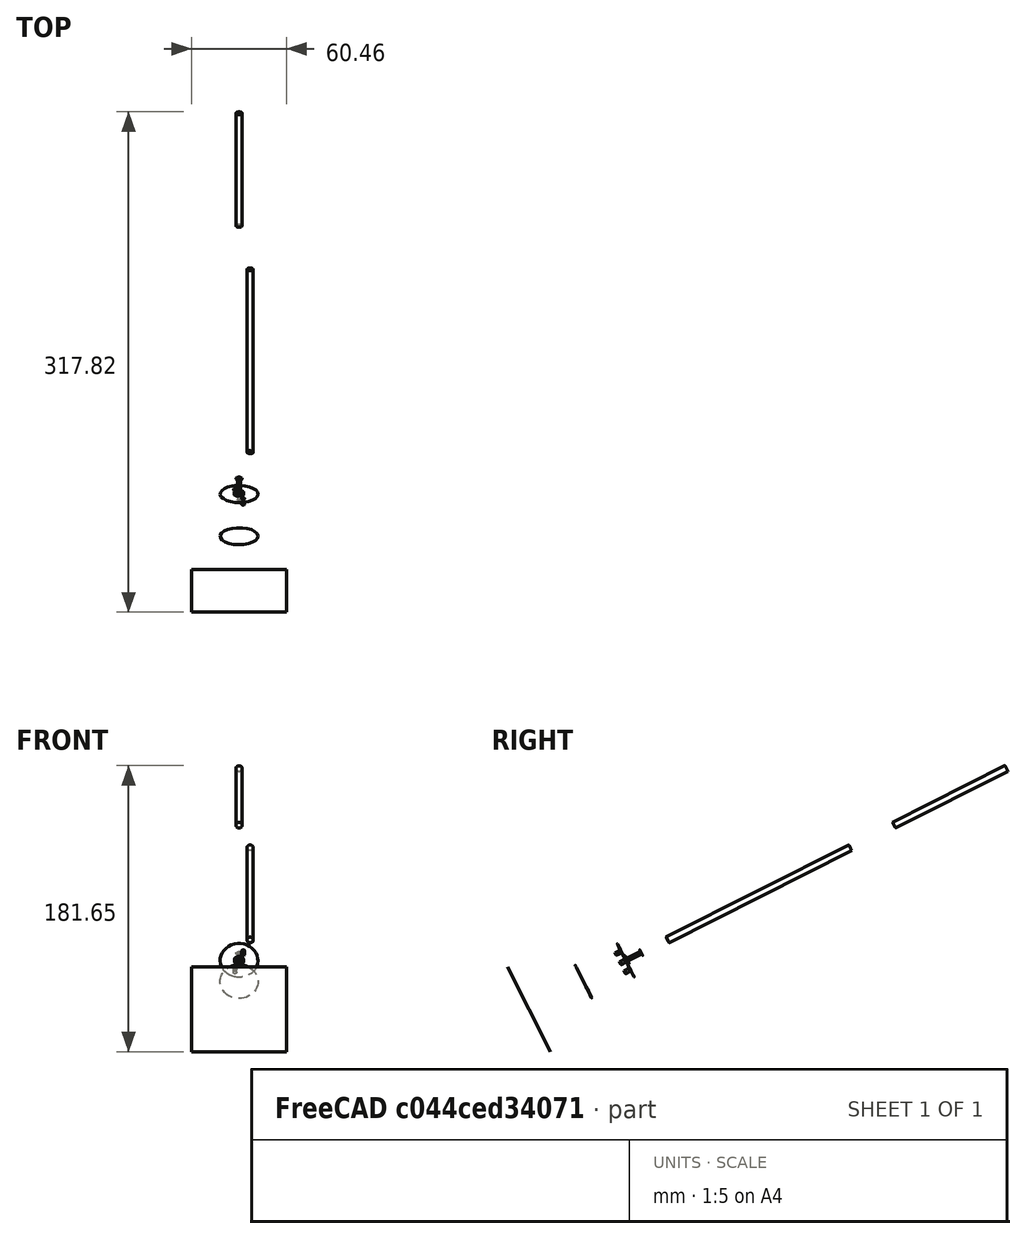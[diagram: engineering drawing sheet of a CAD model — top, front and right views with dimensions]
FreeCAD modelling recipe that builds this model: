
FCSTD DOCUMENT  (FreeCAD 0.19R24366 (Git))
Label: sailface_prop_motor_assembly
License: All rights reserved
LicenseURL: http://en.wikipedia.org/wiki/All_rights_reserved
objects: App::FeaturePython×23, Part::FeaturePython×17, App::Link×4
note: 16 computed .brp shape members not serialized (recipe doc carries the construction recipe); baked Part::Feature solids carry a one-line shape summary decoded from their .brp
EXTERNAL_REF file=Prop_uxcell_prop_shaft.FCStd obj=Part
EXTERNAL_REF file=Prop_uxcell_prop_shaft.FCStd obj=Part001
EXTERNAL_REF file=Prop_uxcell_prop_shaft.FCStd obj=Part002
EXTERNAL_REF file=MotorAndHolder_v1.FCStd obj=Part

FEATURE [App::Link] Link004  label="PropShaftSleeve"
  LinkPlacement = pos=(-1.04194e-10,303.325,152.862) rot=(0.782097,-0.530606,0.326776;2.24386rad)
  LinkedObject = -> <external Prop_uxcell_prop_shaft.FCStd>#Part
  Placement = pos=(-1.04194e-10,303.325,152.862) rot=(0.782097,-0.530606,0.326776;2.24386rad)
FEATURE [App::Link] Link005  label="PropAndShaft"
  LinkPlacement = pos=(1.45925,156.515,79.2819) rot=(0.211549,0.512519,0.832209;3.80335rad)
  LinkedObject = -> <external Prop_uxcell_prop_shaft.FCStd>#Part001
  Placement = pos=(1.45925,156.515,79.2819) rot=(0.211549,0.512519,0.832209;3.80335rad)
FEATURE [App::Link] Link015  label="ShaftConnectorTemp"
  LinkPlacement = pos=(1.74213e-10,0,0) rot=(-0.752268,-0.345496,-0.561003;1.37203rad)
  LinkedObject = -> <external Prop_uxcell_prop_shaft.FCStd>#Part002
  Placement = pos=(1.74213e-10,0,0) rot=(-0.752268,-0.345496,-0.561003;1.37203rad)
FEATURE [App::Link] Link014  label="MotorPart"
  LinkPlacement = pos=(9.7944e-11,0,0) rot=(-0.332635,0.494526,0.802993;2.15114rad)
  LinkedObject = -> <external MotorAndHolder_v1.FCStd>#Part
  Placement = pos=(9.7944e-11,0,0) rot=(-0.332635,0.494526,0.802993;2.15114rad)
FEATURE [Part::FeaturePython] Workplane  # WARN: FeaturePython — macro-defined, semantics opaque (R4)
  Fixed = true
  Length = 60.4603
  Placement = pos=(0,0,0) rot=(1,0,0;2.0376rad)
  Width = 60.4603
FEATURE [Part::FeaturePython] Parts001  # WARN: FeaturePython — macro-defined, semantics opaque (R4)
  Group = -> [Link014,Link015,Link005,Link004,Workplane]
  GroupMode = 0
FEATURE [Part::FeaturePython] _Element043  # link proxy (typed FeaturePython)
  Detach = false
  LinkTransform = true
  LinkedObject = -> Link004 [Extrude.Face2]
  _Parent = -> Elements001
FEATURE [App::FeaturePython] ElementLink018  label="_Element043"  # link proxy (typed FeaturePython)
  LinkTransform = true
  LinkedObject = -> _Element043
  _Parent = -> Constraint008
FEATURE [Part::FeaturePython] _Element044  # link proxy (typed FeaturePython)
  Detach = false
  LinkTransform = true
  LinkedObject = -> Link005 [Extrude002.Face1]
  _Parent = -> Elements001
FEATURE [App::FeaturePython] ElementLink019  label="_Element044"  # link proxy (typed FeaturePython)
  LinkTransform = true
  LinkedObject = -> _Element044
  _Parent = -> Constraint008
FEATURE [App::FeaturePython] Constraint008  label="AxialAlignment002"  # WARN: FeaturePython — macro-defined, semantics opaque (R4)
  Angle = 0
  AnglePitch = 0
  AngleRoll = 0
  Disabled = false
  Group = -> [ElementLink018,ElementLink019]
  LockAngle = false
  Multiply = false
  _ConstraintType = 36
  _Parent = -> Constraints001
FEATURE [App::FeaturePython] ElementLink020  label="_Element044"  # link proxy (typed FeaturePython)
  LinkTransform = true
  LinkedObject = -> _Element044
  _Parent = -> Constraint009
FEATURE [App::FeaturePython] ElementLink021  label="_Element043"  # link proxy (typed FeaturePython)
  LinkTransform = true
  LinkedObject = -> _Element043
  _Parent = -> Constraint009
FEATURE [App::FeaturePython] Constraint009  label="AxialAlignment"  # WARN: FeaturePython — macro-defined, semantics opaque (R4)
  Angle = 0
  AnglePitch = 0
  AngleRoll = 0
  Disabled = false
  Group = -> [ElementLink020,ElementLink021]
  LockAngle = false
  Multiply = false
  _ConstraintType = 36
  _Parent = -> Constraints001
FEATURE [Part::FeaturePython] _Element046  # link proxy (typed FeaturePython)
  Detach = false
  LinkTransform = true
  LinkedObject = -> Link005 [Extrude002.Face3]
  _Parent = -> Elements001
FEATURE [Part::FeaturePython] _Element045  # link proxy (typed FeaturePython)
  Detach = false
  LinkTransform = true
  LinkedObject = -> Link015 [Body.Pocket001.Face7]
  _Parent = -> Elements001
FEATURE [Part::FeaturePython] _Element047  # link proxy (typed FeaturePython)
  Detach = false
  LinkTransform = true
  LinkedObject = -> Link014 [Body.Pocket.Face11]
  _Parent = -> Elements001
FEATURE [Part::FeaturePython] _Element048  # link proxy (typed FeaturePython)
  Detach = false
  LinkTransform = true
  LinkedObject = -> Link015 [Body.Pocket001.Face6]
  _Parent = -> Elements001
FEATURE [App::FeaturePython] Constraints001  # WARN: FeaturePython — macro-defined, semantics opaque (R4)
  Group = -> [Constraint008,Constraint009,Constraint,Constraint010,Constraint011,Constraint012,Constraint013]
  _Version = 1
FEATURE [App::FeaturePython] Elements001  # WARN: FeaturePython — macro-defined, semantics opaque (R4)
  Group = -> [_Element043,_Element044,_Element045,_Element046,_Element047,_Element048,Element,Element001,Element002,Element003,Element004,_Element,_Element049,_Element050]
FEATURE [Part::FeaturePython] Assembly001  label="PropMotorAssembly"  # WARN: FeaturePython — macro-defined, semantics opaque (R4)
  AutoRelax = true
  BuildShape = 0
  Freeze = false
  Group = -> [Constraints001,Parts001,Elements001]
  Verbose = false
  _SolverType = 1
  _Version = 1
FEATURE [Part::FeaturePython] Element  # link proxy (typed FeaturePython)
  Detach = false
  LinkTransform = true
  LinkedObject = -> Link014 [Body.Pocket.Face5]
  _Parent = -> Elements001
FEATURE [Part::FeaturePython] Element001  # link proxy (typed FeaturePython)
  Detach = false
  LinkTransform = true
  LinkedObject = -> Link014 [Body.Pocket.Face3]
  _Parent = -> Elements001
FEATURE [Part::FeaturePython] Element002  # link proxy (typed FeaturePython)
  Detach = false
  LinkTransform = true
  LinkedObject = -> Link014 [Body.Pocket.Face10]
  _Parent = -> Elements001
FEATURE [Part::FeaturePython] Element003  # link proxy (typed FeaturePython)
  Detach = false
  LinkTransform = true
  LinkedObject = -> Link014 [Body.Pocket.Face6]
  _Parent = -> Elements001
FEATURE [Part::FeaturePython] Element004  # link proxy (typed FeaturePython)
  Detach = false
  LinkTransform = true
  LinkedObject = -> Link014 [Body.Pocket.Face4]
  _Parent = -> Elements001
FEATURE [App::FeaturePython] Constraint  label="AxialAlignment003"  # WARN: FeaturePython — macro-defined, semantics opaque (R4)
  Angle = 0
  AnglePitch = 0
  AngleRoll = 0
  Disabled = false
  Group = -> [ElementLink,ElementLink022]
  LockAngle = false
  Multiply = false
  _ConstraintType = 36
  _Parent = -> Constraints001
FEATURE [App::FeaturePython] ElementLink  label="_Element"  # link proxy (typed FeaturePython)
  LinkTransform = true
  LinkedObject = -> _Element
  _Parent = -> Constraint
FEATURE [Part::FeaturePython] _Element  # link proxy (typed FeaturePython)
  Detach = false
  LinkTransform = true
  LinkedObject = -> Link015 [Body.Pocket001.Face4]
  _Parent = -> Elements001
FEATURE [App::FeaturePython] ElementLink022  label="Element002"  # link proxy (typed FeaturePython)
  LinkTransform = true
  LinkedObject = -> Element002
  _Parent = -> Constraint
FEATURE [App::FeaturePython] Constraint010  label="AxialAlignment004"  # WARN: FeaturePython — macro-defined, semantics opaque (R4)
  Angle = 0
  AnglePitch = 0
  AngleRoll = 0
  Disabled = false
  Group = -> [ElementLink023,ElementLink024]
  LockAngle = false
  Multiply = false
  _ConstraintType = 36
  _Parent = -> Constraints001
FEATURE [App::FeaturePython] ElementLink023  label="_Element044"  # link proxy (typed FeaturePython)
  LinkTransform = true
  LinkedObject = -> _Element044
  _Parent = -> Constraint010
FEATURE [App::FeaturePython] ElementLink024  label="_Element"  # link proxy (typed FeaturePython)
  LinkTransform = true
  LinkedObject = -> _Element
  _Parent = -> Constraint010
FEATURE [App::FeaturePython] Constraint011  label="AxialAlignment005"  # WARN: FeaturePython — macro-defined, semantics opaque (R4)
  Angle = 0
  AnglePitch = 0
  AngleRoll = 0
  Disabled = false
  Group = -> [ElementLink025,ElementLink026]
  LockAngle = false
  Multiply = false
  _ConstraintType = 36
  _Parent = -> Constraints001
FEATURE [App::FeaturePython] ElementLink025  label="_Element049"  # link proxy (typed FeaturePython)
  LinkTransform = true
  LinkedObject = -> _Element049
  _Parent = -> Constraint011
FEATURE [Part::FeaturePython] _Element049  # link proxy (typed FeaturePython)
  Detach = false
  LinkTransform = true
  LinkedObject = -> Workplane [Face1]
  _Parent = -> Elements001
FEATURE [App::FeaturePython] ElementLink026  label="_Element050"  # link proxy (typed FeaturePython)
  LinkTransform = true
  LinkedObject = -> _Element050
  _Parent = -> Constraint011
FEATURE [Part::FeaturePython] _Element050  # link proxy (typed FeaturePython)
  Detach = false
  LinkTransform = true
  LinkedObject = -> Link014 [Body.Pocket.Face2]
  _Parent = -> Elements001
FEATURE [App::FeaturePython] Constraint012  label="PlaneCoincident"  # WARN: FeaturePython — macro-defined, semantics opaque (R4)
  Angle = 0
  AnglePitch = 0
  AngleRoll = 0
  Cascade = false
  Disabled = false
  Group = -> [ElementLink027,ElementLink028]
  LockAngle = false
  Multiply = false
  OffsetX = 0
  OffsetY = 0
  _ConstraintType = 35
  _Parent = -> Constraints001
FEATURE [App::FeaturePython] ElementLink027  label="_Element047"  # link proxy (typed FeaturePython)
  LinkTransform = true
  LinkedObject = -> _Element047
  _Parent = -> Constraint012
FEATURE [App::FeaturePython] ElementLink028  label="_Element045"  # link proxy (typed FeaturePython)
  LinkTransform = true
  LinkedObject = -> _Element045
  _Parent = -> Constraint012
FEATURE [App::FeaturePython] Constraint013  label="PlaneCoincident001"  # WARN: FeaturePython — macro-defined, semantics opaque (R4)
  Angle = 0
  AnglePitch = 0
  AngleRoll = 0
  Cascade = false
  Disabled = true
  Group = -> [ElementLink029,ElementLink030]
  LockAngle = false
  Multiply = false
  OffsetX = 0
  OffsetY = 0
  _ConstraintType = 35
  _Parent = -> Constraints001
FEATURE [App::FeaturePython] ElementLink029  label="_Element046"  # link proxy (typed FeaturePython)
  LinkTransform = true
  LinkedObject = -> _Element046
  _Parent = -> Constraint013
FEATURE [App::FeaturePython] ElementLink030  label="_Element045"  # link proxy (typed FeaturePython)
  LinkTransform = true
  LinkedObject = -> _Element045
  _Parent = -> Constraint013

RESOLVED EXTERNAL PARTS (link-assembly join: the EXTERNAL_REF files above that resolve inside this repo's crawl, each included once):
---- part MotorAndHolder_v1.FCStd = doc fcstd_ec45f42837d4 ----
FCSTD DOCUMENT  (FreeCAD 0.19R24366 (Git))
Label: MotorAndHolder_v1
License: All rights reserved
LicenseURL: http://en.wikipedia.org/wiki/All_rights_reserved
objects: Sketcher::SketchObject×16, PartDesign::Pad×9, PartDesign::Pocket×9, PartDesign::Body×4, App::Part×4, Mesh::Feature×1
note: 56 computed .brp shape members not serialized (recipe doc carries the construction recipe); baked Part::Feature solids carry a one-line shape summary decoded from their .brp

FEATURE [Sketcher::SketchObject] Sketch
  FullyConstrained = false
  MapMode = 5
  Support = -> [XY_Plane001]
  sketch-geometry (1):
    g0: Circle CenterX=0 CenterY=0 CenterZ=0 NormalX=0 NormalY=0 NormalZ=1 AngleXU=0 Radius=12
  constraints (1):
    c: Radius(g0) = 12
FEATURE [PartDesign::Pad] Pad  label="MotorMain"
  Direction = (1,1,1)
  Length = 30
  Length2 = 100
  Profile = -> Sketch
  Type = 0
FEATURE [Sketcher::SketchObject] Sketch001
  FullyConstrained = true
  MapMode = 5
  Placement = pos=(0,0,30) rot=(0,0,1;0rad)
  Support = -> [Pad]
  sketch-geometry (1):
    g0: Circle CenterX=0 CenterY=0 CenterZ=0 NormalX=0 NormalY=0 NormalZ=1 AngleXU=0 Radius=3
  constraints (2):
    c: Coincident(g0,g-1)
    c: Radius(g0) = 3
FEATURE [PartDesign::Pad] Pad001  label="MotorHeader"
  BaseFeature = -> Pad
  Direction = (1,1,1)
  Length = 1
  Length2 = 100
  Profile = -> Sketch001
  Type = 0
FEATURE [Sketcher::SketchObject] Sketch002
  FullyConstrained = true
  MapMode = 5
  Placement = pos=(0,0,31) rot=(0,0,1;0rad)
  Support = -> [Pad001]
  sketch-geometry (1):
    g0: Circle CenterX=0 CenterY=0 CenterZ=0 NormalX=0 NormalY=0 NormalZ=1 AngleXU=0 Radius=1
  constraints (2):
    c: Coincident(g0,g-1)
    c: Radius(g0) = 1
FEATURE [PartDesign::Pad] Pad002  label="Shaft"
  BaseFeature = -> Pad001
  Direction = (1,1,1)
  Length = 10
  Length2 = 100
  Profile = -> Sketch002
  Type = 0
FEATURE [Sketcher::SketchObject] Sketch003
  FullyConstrained = true
  MapMode = 5
  Placement = pos=(0,0,30) rot=(0,0,1;0rad)
  Support = -> [Pad002]
  sketch-geometry (4):
    g0: Circle CenterX=-7 CenterY=0 CenterZ=0 NormalX=0 NormalY=0 NormalZ=1 AngleXU=0 Radius=1
    g1: Circle CenterX=7 CenterY=0 CenterZ=0 NormalX=0 NormalY=0 NormalZ=1 AngleXU=0 Radius=1
    g2: LineSegment StartX=-7 StartY=0 StartZ=0 EndX=0 EndY=0 EndZ=0
    g3: LineSegment StartX=0 StartY=0 StartZ=0 EndX=7 EndY=0 EndZ=0
  constraints (10):
    c: PointOnObject(g0,g-1)
    c: PointOnObject(g1,g-1)
    c: Diameter(g1) = 2
    c: Diameter(g0) = 2
    c: Coincident(g2,g0)
    c: Coincident(g2,g-1)
    c: Coincident(g3,g2)
    c: Coincident(g3,g1)
    c: Equal(g3,g2)
    c: DistanceX(g2,g2) = 7
FEATURE [PartDesign::Pocket] Pocket
  BaseFeature = -> Pad002
  Length = 4
  Length2 = 100
  Profile = -> Sketch003
  Type = 0
FEATURE [PartDesign::Body] Body  label="MotorBody"
  Group = -> [Sketch,Pad,Sketch001,Pad001,Sketch002,Pad002,Sketch003,Pocket]
  Origin = -> Origin001
  Tip = -> Pocket
FEATURE [App::Part] Part  label="MotorPart"
  Group = -> [Body]
  Origin = -> Origin
FEATURE [Sketcher::SketchObject] Sketch004
  FullyConstrained = false
  Placement = pos=(0,0,30) rot=(0,0,1;0rad)
  sketch-geometry (6):
    g0: LineSegment StartX=-15 StartY=2.95461 StartZ=0 EndX=15 EndY=2.95461 EndZ=0
    g1: LineSegment StartX=15 StartY=2.95461 StartZ=0 EndX=15 EndY=-13.0454 EndZ=0
    g2: LineSegment StartX=15 StartY=-13.0454 StartZ=0 EndX=-15 EndY=-13.0454 EndZ=0
    g3: LineSegment StartX=-15 StartY=-13.0454 StartZ=0 EndX=-15 EndY=2.95461 EndZ=0
    g4: LineSegment StartX=-15 StartY=0 StartZ=0 EndX=0 EndY=0 EndZ=0
    g5: LineSegment StartX=0 StartY=0 StartZ=0 EndX=15 EndY=0 EndZ=0
  constraints (17):
    c: Coincident(g0,g1)
    c: Coincident(g1,g2)
    c: Coincident(g2,g3)
    c: Coincident(g3,g0)
    c: Horizontal(g0)
    c: Horizontal(g2)
    c: Vertical(g1)
    c: Vertical(g3)
    c: DistanceY(g1,g1) = 16
    c: DistanceX(g0,g0) = 30
    c: PointOnObject(g4,g3)
    c: Coincident(g4,g-1)
    c: Horizontal(g4)
    c: PointOnObject(g5,g1)
    c: Horizontal(g5)
    c: Equal(g4,g5)
    c: Coincident(g5,g-1)
FEATURE [PartDesign::Pad] Pad003
  Direction = (1,1,1)
  Length = 2
  Length2 = 100
  Placement = pos=(0,0,30) rot=(0,0,1;0rad)
  Profile = -> Sketch004
  Type = 0
FEATURE [Sketcher::SketchObject] Sketch005
  FullyConstrained = true
  MapMode = 5
  Placement = pos=(0,0,30) rot=(0,0,1;0rad)
  Support = -> [Pad]
  sketch-geometry (1):
    g0: Circle CenterX=0 CenterY=0 CenterZ=0 NormalX=0 NormalY=0 NormalZ=1 AngleXU=0 Radius=3.4
  constraints (2):
    c: Coincident(g0,g-1)
    c: Radius(g0) = 3.4
FEATURE [PartDesign::Pocket] Pocket001
  BaseFeature = -> Pad003
  Length = 20
  Length2 = 100
  Placement = pos=(0,0,30) rot=(0,0,1;0rad)
  Profile = -> Sketch005
  Reversed = true
  Type = 0
FEATURE [PartDesign::Pad] Pad004
  BaseFeature = -> Pocket001
  Direction = (1,1,1)
  Length = 25
  Length2 = 100
  Placement = pos=(0,0,30) rot=(0,0,1;0rad)
  Profile = -> Sketch004
  Reversed = true
  Type = 0
FEATURE [Sketcher::SketchObject] Sketch006
  FullyConstrained = false
  MapMode = 5
  Support = -> [XY_Plane003]
  sketch-geometry (1):
    g0: Circle CenterX=0 CenterY=0 CenterZ=0 NormalX=0 NormalY=0 NormalZ=1 AngleXU=0 Radius=12.2
  constraints (1):
    c: Radius(g0) = 12.2
FEATURE [PartDesign::Pocket] Pocket002
  BaseFeature = -> Pad004
  Length = 30
  Length2 = 100
  Placement = pos=(0,0,30) rot=(0,0,1;0rad)
  Profile = -> Sketch006
  Reversed = true
  Type = 0
FEATURE [Sketcher::SketchObject] Sketch007
  FullyConstrained = false
  MapMode = 5
  Placement = pos=(0,0,32) rot=(0,0,1;0rad)
  Support = -> [Pocket002]
  sketch-geometry (4):
    g0: Circle CenterX=-7.01627 CenterY=0 CenterZ=0 NormalX=0 NormalY=0 NormalZ=1 AngleXU=0 Radius=1.2
    g1: Circle CenterX=7.01627 CenterY=0 CenterZ=0 NormalX=0 NormalY=0 NormalZ=1 AngleXU=0 Radius=1.1
    g2: LineSegment StartX=-7.01627 StartY=0 StartZ=0 EndX=0 EndY=0 EndZ=0
    g3: LineSegment StartX=0 StartY=0 StartZ=0 EndX=7.01627 EndY=0 EndZ=0
  constraints (9):
    c: PointOnObject(g0,g-1)
    c: PointOnObject(g1,g-1)
    c: Diameter(g1) = 2.2
    c: Diameter(g0) = 2.4
    c: Coincident(g2,g0)
    c: Coincident(g2,g-1)
    c: Coincident(g3,g2)
    c: Coincident(g3,g1)
    c: Equal(g3,g2)
FEATURE [PartDesign::Pocket] Pocket003
  BaseFeature = -> Pocket002
  Length = 5
  Length2 = 100
  Placement = pos=(0,0,30) rot=(0,0,1;0rad)
  Profile = -> Sketch007
  Type = 0
FEATURE [Sketcher::SketchObject] Sketch008
  FullyConstrained = false
  MapMode = 5
  Placement = pos=(0,0,32) rot=(0,0,1;0rad)
  Support = -> [Pocket003]
  sketch-geometry (4):
    g0: Circle CenterX=-10 CenterY=-10.9518 CenterZ=0 NormalX=0 NormalY=0 NormalZ=1 AngleXU=0 Radius=1.4
    g1: Circle CenterX=10 CenterY=-10.9518 CenterZ=0 NormalX=0 NormalY=0 NormalZ=1 AngleXU=0 Radius=1.4
    g2: LineSegment StartX=10 StartY=-10.9518 StartZ=0 EndX=0 EndY=-10.9518 EndZ=0
    g3: LineSegment StartX=-10 StartY=-10.9518 StartZ=0 EndX=0 EndY=-10.9518 EndZ=0
  constraints (10):
    c: Horizontal(g1,g0)
    c: Coincident(g2,g1)
    c: PointOnObject(g2,g-2)
    c: Horizontal(g2)
    c: Coincident(g3,g0)
    c: Coincident(g3,g2)
    c: Equal(g2,g3)
    c: DistanceX(g0,g1) = 20
    c: Equal(g0,g1)
    c: Diameter(g0) = 2.8
FEATURE [PartDesign::Pocket] Pocket004
  BaseFeature = -> Pocket003
  Length = 50
  Length2 = 100
  Placement = pos=(0,0,30) rot=(0,0,1;0rad)
  Profile = -> Sketch008
  Type = 0
FEATURE [PartDesign::Body] Body001  label="MotorHolderBody"
  Group = -> [Sketch004,Pad003,Sketch005,Pocket001,Pad004,Sketch006,Pocket002,Sketch007,Pocket003,Sketch008,Pocket004]
  Origin = -> Origin003
  Tip = -> Pocket004
FEATURE [App::Part] Part001  label="MotorHolder"
  Group = -> [Body001]
  Origin = -> Origin002
FEATURE [Mesh::Feature] Mesh  label="MotorHolder (Meshed)"
FEATURE [Sketcher::SketchObject] Sketch013
  FullyConstrained = true
  MapMode = 5
  Support = -> [XY_Plane012]
  sketch-geometry (1):
    g0: Circle CenterX=0 CenterY=0 CenterZ=0 NormalX=0 NormalY=0 NormalZ=1 AngleXU=0 Radius=1.25
  constraints (2):
    c: Coincident(g0,g-1)
    c: Diameter(g0) = 2.5
FEATURE [PartDesign::Pad] Pad006
  Direction = (1,1,1)
  Length = 200
  Length2 = 100
  Profile = -> Sketch013
  Type = 0
FEATURE [PartDesign::Body] Body006
  Group = -> [Sketch013,Pad006]
  Origin = -> Origin012
  Tip = -> Pad006
FEATURE [App::Part] Part006  label="ConnectorRod2.5x200mm001"
  Group = -> [Body006]
  Origin = -> Origin013
FEATURE [Sketcher::SketchObject] Sketch014
  FullyConstrained = false
  MapMode = 5
  Support = -> [XY_Plane015]
  sketch-geometry (1):
    g0: Circle CenterX=0 CenterY=0 CenterZ=0 NormalX=0 NormalY=0 NormalZ=1 AngleXU=0 Radius=12
  constraints (1):
    c: Radius(g0) = 12
FEATURE [PartDesign::Pad] Pad007  label="MotorMain001"
  Direction = (1,1,1)
  Length = 30
  Length2 = 100
  Profile = -> Sketch014
  Type = 0
FEATURE [Sketcher::SketchObject] Sketch017
  FullyConstrained = false
  Placement = pos=(0,0,30) rot=(0,0,1;0rad)
  sketch-geometry (6):
    g0: LineSegment StartX=-15 StartY=2.95461 StartZ=0 EndX=15 EndY=2.95461 EndZ=0
    g1: LineSegment StartX=15 StartY=2.95461 StartZ=0 EndX=15 EndY=-13.0454 EndZ=0
    g2: LineSegment StartX=15 StartY=-13.0454 StartZ=0 EndX=-15 EndY=-13.0454 EndZ=0
    g3: LineSegment StartX=-15 StartY=-13.0454 StartZ=0 EndX=-15 EndY=2.95461 EndZ=0
    g4: LineSegment StartX=-15 StartY=0 StartZ=0 EndX=0 EndY=0 EndZ=0
    g5: LineSegment StartX=0 StartY=0 StartZ=0 EndX=15 EndY=0 EndZ=0
  constraints (17):
    c: Coincident(g0,g1)
    c: Coincident(g1,g2)
    c: Coincident(g2,g3)
    c: Coincident(g3,g0)
    c: Horizontal(g0)
    c: Horizontal(g2)
    c: Vertical(g1)
    c: Vertical(g3)
    c: DistanceY(g1,g1) = 16
    c: DistanceX(g0,g0) = 30
    c: PointOnObject(g4,g3)
    c: Coincident(g4,g-1)
    c: Horizontal(g4)
    c: PointOnObject(g5,g1)
    c: Horizontal(g5)
    c: Equal(g4,g5)
    c: Coincident(g5,g-1)
FEATURE [PartDesign::Pad] Pad008
  Direction = (1,1,1)
  Length = 2
  Length2 = 100
  Placement = pos=(0,0,30) rot=(0,0,1;0rad)
  Profile = -> Sketch017
  Type = 0
FEATURE [Sketcher::SketchObject] Sketch018
  FullyConstrained = true
  MapMode = 5
  Placement = pos=(0,0,30) rot=(0,0,1;0rad)
  Support = -> [Pad007]
  sketch-geometry (1):
    g0: Circle CenterX=0 CenterY=0 CenterZ=0 NormalX=0 NormalY=0 NormalZ=1 AngleXU=0 Radius=3.4
  constraints (2):
    c: Coincident(g0,g-1)
    c: Radius(g0) = 3.4
FEATURE [PartDesign::Pocket] Pocket008
  BaseFeature = -> Pad008
  Length = 20
  Length2 = 100
  Placement = pos=(0,0,30) rot=(0,0,1;0rad)
  Profile = -> Sketch018
  Reversed = true
  Type = 0
FEATURE [PartDesign::Pad] Pad009
  BaseFeature = -> Pocket008
  Direction = (1,1,1)
  Length = 25
  Length2 = 100
  Placement = pos=(0,0,30) rot=(0,0,1;0rad)
  Profile = -> Sketch017
  Reversed = true
  Type = 0
FEATURE [Sketcher::SketchObject] Sketch019
  FullyConstrained = false
  MapMode = 5
  Support = -> [XY_Plane016]
  sketch-geometry (1):
    g0: Circle CenterX=0 CenterY=0 CenterZ=0 NormalX=0 NormalY=0 NormalZ=1 AngleXU=0 Radius=12.2
  constraints (1):
    c: Radius(g0) = 12.2
FEATURE [PartDesign::Pocket] Pocket005
  BaseFeature = -> Pad009
  Length = 30
  Length2 = 100
  Placement = pos=(0,0,30) rot=(0,0,1;0rad)
  Profile = -> Sketch019
  Reversed = true
  Type = 0
FEATURE [Sketcher::SketchObject] Sketch015
  FullyConstrained = false
  MapMode = 5
  Placement = pos=(0,0,32) rot=(0,0,1;0rad)
  Support = -> [Pocket005]
  sketch-geometry (4):
    g0: Circle CenterX=-7.01627 CenterY=0 CenterZ=0 NormalX=0 NormalY=0 NormalZ=1 AngleXU=0 Radius=1.2
    g1: Circle CenterX=7.01627 CenterY=0 CenterZ=0 NormalX=0 NormalY=0 NormalZ=1 AngleXU=0 Radius=1.1
    g2: LineSegment StartX=-7.01627 StartY=0 StartZ=0 EndX=0 EndY=0 EndZ=0
    g3: LineSegment StartX=0 StartY=0 StartZ=0 EndX=7.01627 EndY=0 EndZ=0
  constraints (9):
    c: PointOnObject(g0,g-1)
    c: PointOnObject(g1,g-1)
    c: Diameter(g1) = 2.2
    c: Diameter(g0) = 2.4
    c: Coincident(g2,g0)
    c: Coincident(g2,g-1)
    c: Coincident(g3,g2)
    c: Coincident(g3,g1)
    c: Equal(g3,g2)
FEATURE [PartDesign::Pocket] Pocket006
  BaseFeature = -> Pocket005
  Length = 5
  Length2 = 100
  Placement = pos=(0,0,30) rot=(0,0,1;0rad)
  Profile = -> Sketch015
  Type = 0
FEATURE [Sketcher::SketchObject] Sketch016
  FullyConstrained = false
  MapMode = 5
  Placement = pos=(0,0,32) rot=(0,0,1;0rad)
  Support = -> [Pocket006]
  sketch-geometry (4):
    g0: Circle CenterX=-10 CenterY=-10.9518 CenterZ=0 NormalX=0 NormalY=0 NormalZ=1 AngleXU=0 Radius=1.4
    g1: Circle CenterX=10 CenterY=-10.9518 CenterZ=0 NormalX=0 NormalY=0 NormalZ=1 AngleXU=0 Radius=1.4
    g2: LineSegment StartX=10 StartY=-10.9518 StartZ=0 EndX=0 EndY=-10.9518 EndZ=0
    g3: LineSegment StartX=-10 StartY=-10.9518 StartZ=0 EndX=0 EndY=-10.9518 EndZ=0
  constraints (10):
    c: Horizontal(g1,g0)
    c: Coincident(g2,g1)
    c: PointOnObject(g2,g-2)
    c: Horizontal(g2)
    c: Coincident(g3,g0)
    c: Coincident(g3,g2)
    c: Equal(g2,g3)
    c: DistanceX(g0,g1) = 20
    c: Equal(g0,g1)
    c: Diameter(g0) = 2.8
FEATURE [PartDesign::Pocket] Pocket007
  BaseFeature = -> Pocket006
  Length = 50
  Length2 = 100
  Placement = pos=(0,0,30) rot=(0,0,1;0rad)
  Profile = -> Sketch016
  Type = 0
FEATURE [PartDesign::Body] Body007  label="MotorHolderBody001"
  Group = -> [Sketch017,Pad008,Sketch018,Pocket008,Pad009,Sketch019,Pocket005,Sketch015,Pocket006,Sketch016,Pocket007]
  Origin = -> Origin014
  Tip = -> Pocket007
FEATURE [App::Part] Part007  label="MotorHolder001"
  Group = -> [Body007]
  Origin = -> Origin015
---- part Prop_uxcell_prop_shaft.FCStd = doc fcstd_5d733dbdb6b5 ----
FCSTD DOCUMENT  (FreeCAD 0.19R24366 (Git))
Label: Prop_uxcell_prop_shaft
License: All rights reserved
LicenseURL: http://en.wikipedia.org/wiki/All_rights_reserved
objects: Sketcher::SketchObject×6, Part::Extrusion×3, App::Part×3, PartDesign::Pocket×2, Mesh::Feature×1, PartDesign::Pad×1, PartDesign::Body×1
note: 16 computed .brp shape members not serialized (recipe doc carries the construction recipe); baked Part::Feature solids carry a one-line shape summary decoded from their .brp

FEATURE [Mesh::Feature] driveshaft
FEATURE [Sketcher::SketchObject] Sketch
  FullyConstrained = true
  sketch-geometry (2):
    g0: Circle CenterX=0 CenterY=0 CenterZ=0 NormalX=0 NormalY=0 NormalZ=1 AngleXU=0 Radius=3
    g1: Circle CenterX=0 CenterY=0 CenterZ=0 NormalX=0 NormalY=0 NormalZ=1 AngleXU=0 Radius=2
  constraints (4):
    c: Coincident(g0,g1)
    c: Coincident(g0,g-1)
    c: Diameter(g1) = 4
    c: Diameter(g0) = 6
FEATURE [Part::Extrusion] Extrude  label="PropShaftSleeve001"
  Base = -> Sketch
  Dir = (0,0,1)
  DirMode = 0
  FaceMakerClass = Part::FaceMakerBullseye
  LengthFwd = 80
  LengthRev = 0
  Solid = true
  Symmetric = false
FEATURE [App::Part] Part  label="PropShaftSleeve"
  Group = -> [Sketch,Extrude]
  Origin = -> Origin
FEATURE [Sketcher::SketchObject] Sketch001
  FullyConstrained = false
  sketch-geometry (8):
    g0: Circle CenterX=0 CenterY=0 CenterZ=0 NormalX=0 NormalY=0 NormalZ=1 AngleXU=0 Radius=3
    g1: LineSegment StartX=-2.96858 StartY=0.433018 StartZ=0 EndX=-0.480038 EndY=17.4934 EndZ=0
    g2: LineSegment StartX=2.15757 StartY=2.08444 StartZ=0 EndX=-0.480038 EndY=17.4934 EndZ=0
    g3: LineSegment StartX=-2.96858 StartY=0.433018 StartZ=0 EndX=-16.5261 EndY=-5.75668 EndZ=0
    g4: LineSegment StartX=-16.5261 StartY=-5.75668 StartZ=0 EndX=-0.463294 EndY=-3.11641 EndZ=0
    g5: LineSegment StartX=-0.463294 StartY=-3.11641 StartZ=0 EndX=14.1368 EndY=-10.3151 EndZ=0
    g6: LineSegment StartX=14.1368 StartY=-10.3151 StartZ=0 EndX=2.15757 EndY=2.08444 EndZ=0
    g7: Circle CenterX=0 CenterY=0 CenterZ=0 NormalX=0 NormalY=0 NormalZ=1 AngleXU=0 Radius=17.5
  constraints (19):
    c: Coincident(g0,g-1)
    c: Diameter(g0) = 6
    c: PointOnObject(g1,g0)
    c: PointOnObject(g2,g0)
    c: Coincident(g2,g1)
    c: Coincident(g4,g3)
    c: Coincident(g4,g5)
    c: Tangent(g5,g0)
    c: Tangent(g4,g0)
    c: Coincident(g3,g1)
    c: Coincident(g2,g6)
    c: Coincident(g7,g0)
    c: PointOnObject(g5,g7)
    c: PointOnObject(g3,g7)
    c: PointOnObject(g1,g7)
    c: Coincident(g6,g5)
    c: Diameter(g7) = 35
    c: Tangent(g0,g1,g1) = 1.5708
    c: Tangent(g6,g0,g2) = -1.5708
FEATURE [Part::Extrusion] Extrude001  label="PropMock"
  Base = -> Sketch001
  Dir = (0,0,-1)
  DirMode = 0
  FaceMakerClass = Part::FaceMakerBullseye
  LengthFwd = 3
  LengthRev = 0
  Solid = true
  Symmetric = false
FEATURE [Sketcher::SketchObject] Sketch002
  FullyConstrained = true
  sketch-geometry (1):
    g0: Circle CenterX=0 CenterY=0 CenterZ=0 NormalX=0 NormalY=0 NormalZ=1 AngleXU=0 Radius=2
  constraints (2):
    c: Coincident(g0,g-1)
    c: Diameter(g0) = 4
FEATURE [Part::Extrusion] Extrude002  label="PropShaft"
  Base = -> Sketch002
  Dir = (0,0,-1)
  DirMode = 0
  FaceMakerClass = Part::FaceMakerBullseye
  LengthFwd = 130
  LengthRev = 0
  Solid = true
  Symmetric = false
FEATURE [App::Part] Part001  label="PropAndShaft"
  Group = -> [Sketch001,Extrude001,Sketch002,Extrude002]
  Origin = -> Origin001
FEATURE [Sketcher::SketchObject] Sketch003
  FullyConstrained = true
  MapMode = 5
  Support = -> [XY_Plane003]
  sketch-geometry (1):
    g0: Circle CenterX=0 CenterY=0 CenterZ=0 NormalX=0 NormalY=0 NormalZ=1 AngleXU=0 Radius=3
  constraints (2):
    c: Coincident(g0,g-1)
    c: Diameter(g0) = 6
FEATURE [PartDesign::Pad] Pad
  Direction = (1,1,1)
  Length = 20
  Length2 = 100
  Profile = -> Sketch003
  Type = 0
FEATURE [Sketcher::SketchObject] Sketch004
  FullyConstrained = true
  MapMode = 5
  Placement = pos=(0,0,20) rot=(0,0,1;0rad)
  Support = -> [Pad]
  sketch-geometry (1):
    g0: Circle CenterX=0 CenterY=0 CenterZ=0 NormalX=0 NormalY=0 NormalZ=1 AngleXU=0 Radius=2
  constraints (2):
    c: Coincident(g0,g-1)
    c: Diameter(g0) = 4
FEATURE [PartDesign::Pocket] Pocket
  BaseFeature = -> Pad
  Length = 5
  Length2 = 100
  Profile = -> Sketch004
  Type = 0
FEATURE [Sketcher::SketchObject] Sketch005
  FullyConstrained = true
  MapMode = 5
  Placement = pos=(0,0,0) rot=(1,0,0;3.14159rad)
  Support = -> [Pocket]
  sketch-geometry (1):
    g0: Circle CenterX=0 CenterY=0 CenterZ=0 NormalX=0 NormalY=0 NormalZ=1 AngleXU=0 Radius=1
  constraints (2):
    c: Coincident(g0,g-1)
    c: Diameter(g0) = 2
FEATURE [PartDesign::Pocket] Pocket001
  BaseFeature = -> Pocket
  Length = 5
  Length2 = 100
  Profile = -> Sketch005
  Type = 0
FEATURE [PartDesign::Body] Body
  Group = -> [Sketch003,Pad,Sketch004,Pocket,Sketch005,Pocket001]
  Origin = -> Origin003
  Tip = -> Pocket001
FEATURE [App::Part] Part002  label="ShaftConnectorTemp"
  Group = -> [Body]
  Origin = -> Origin002
